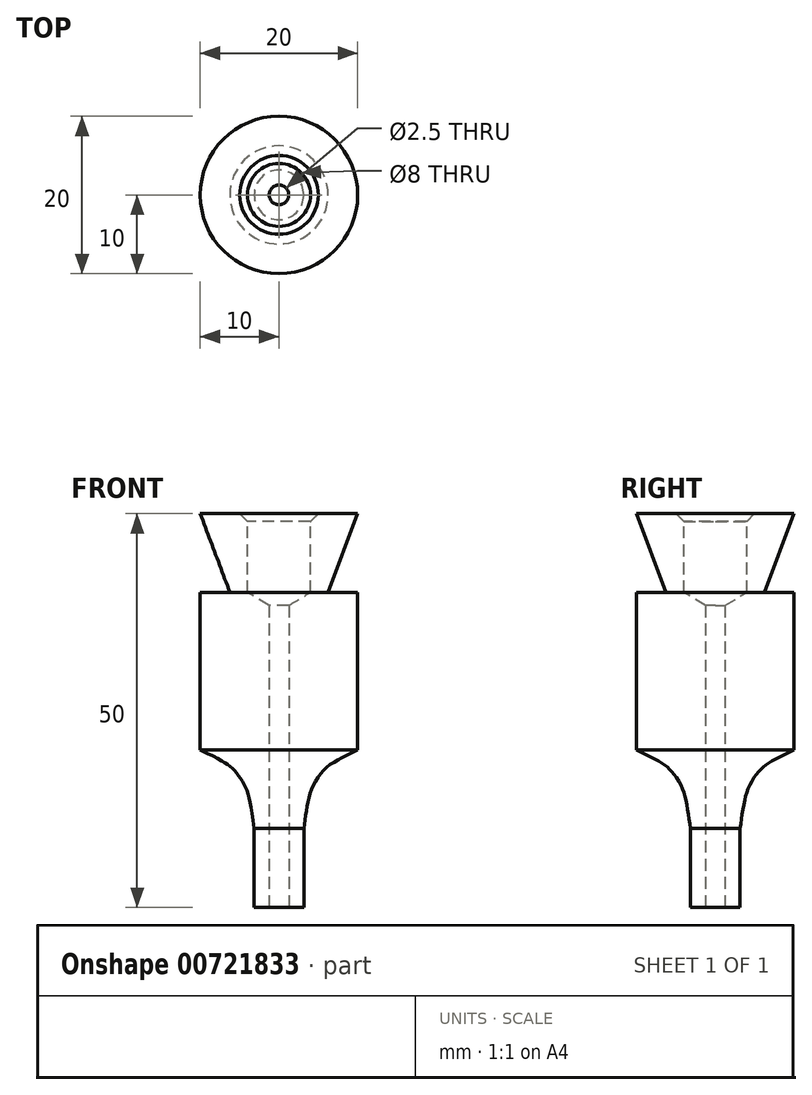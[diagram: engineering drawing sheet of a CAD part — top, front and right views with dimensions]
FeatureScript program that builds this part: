
annotation { "Feature Type Name" : "Feature", "Feature Type Description" : "" }
export const myFeature = defineFeature(function(context is Context, id is Id, definition is map)
    precondition{}
    {
        {
            var Q0;
            Q0=qCreatedBy(makeId("Front.planeOp"),FACE);
            var sketch = newSketch(context, id + "F0", { "sketchPlane" : qUnion([Q0])});
            skLineSegment(sketch, "E0", {"start": v(10, 0) * mm, "end": v(6.24, -10) * mm});
            skLineSegment(sketch, "E1", {"start": v(6.24, -10) * mm, "end": v(10, -10) * mm});
            skLineSegment(sketch, "E2", {"start": v(10, -10) * mm, "end": v(10, -30) * mm});
            skLineSegment(sketch, "E3", {"start": v(3.15, -50) * mm, "end": v(0, -50) * mm});
            skLineSegment(sketch, "E4", {"start": v(0, -50) * mm, "end": v(0, 0) * mm});
            skLineSegment(sketch, "E5", {"start": v(3.15, -50) * mm, "end": v(3.15, -30) * mm});
            skLineSegment(sketch, "E6", {"start": v(3.15, -30) * mm, "end": v(10, -30) * mm});
            skLineSegment(sketch, "E7", {"start": v(10, -10) * mm, "end": v(10, 0) * mm, "construction": true});
            skLineSegment(sketch, "E8", {"start": v(10, 0) * mm, "end": v(0, 0) * mm});
            skFitSpline(sketch, "E9", {"points": [v(10, -30) * mm, v(5.88, -32.4) * mm, v(4.43, -34.37) * mm, v(3.15, -40) * mm], "startDerivative": vector(-21.91, -10.8) * mm, "endDerivative": vector(-3.54, -25.17) * mm});
            skSolve(sketch);
        }
        {
            var Q0;
            Q0 = qSketchRegion(id + "F0", true);
            var Q1;
            Q1=sQuery(id+"F0.wireOp",EDGE,"E4");
            revolve(context, id + "F1", {"surfaceOperationType" : NewSurfaceOperationType.NEW, "entities" : qUnion([Q0]), "axis" : qUnion([Q1]), "revolveType" : RevolveType.FULL});
        }
        {
            var Q0;
            Q0=makeQuery(id+"F1.opRevolve","SWEPT_FACE",FACE,{"disambiguationData":[OSD([sQuery(id+"F0.wireOp",EDGE,"E3")])]});
            var sketch = newSketch(context, id + "F2", { "sketchPlane" : qUnion([Q0])});
            skCircle(sketch, "E10", {"center": v(0, 0) * mm, "radius": 1.25 * mm});
            skSolve(sketch);
        }
        {
            var Q0;
            Q0 = qSketchRegion(id + "F2", true);
            extrude(context, id + "F3", {"entities" : qUnion([Q0]), "operationType" : NewBodyOperationType.REMOVE, "endBound" : BoundingType.THROUGH_ALL, "oppositeDirection" : true, "depth" : 25 * mm, "offsetDistance" : 25 * mm});
        }
        {
            var Q0;
            Q0=makeQuery(id+"F1.opRevolve","SWEPT_FACE",FACE,{"disambiguationData":[OSD([sQuery(id+"F0.wireOp",EDGE,"E3")])]});
            var sketch = newSketch(context, id + "F4", { "sketchPlane" : qUnion([Q0])});
            skCircle(sketch, "E11", {"center": v(0, 0) * mm, "radius": 2 * mm});
            skSolve(sketch);
        }
        {
            var Q0;
            Q0 = qSketchRegion(id + "F4", true);
            extrude(context, id + "F5", {"entities" : qUnion([Q0]), "operationType" : NewBodyOperationType.REMOVE, "depth" : 35 * mm, "offsetDistance" : 25 * mm});
        }
        {
            var Q0;
            Q0=makeQuery(id+"F1.opRevolve","SWEPT_FACE",FACE,{"disambiguationData":[OSD([sQuery(id+"F0.wireOp",EDGE,"E8")])]});
            var sketch = newSketch(context, id + "F6", { "sketchPlane" : qUnion([Q0])});
            skPoint(sketch, "E12", {"position": v(0, 0) * mm});
            skSolve(sketch);
        }
        {
            var Q0;
            Q0=sQuery(id+"F6.wireOp",VERTEX,"E12");
            var Q1;
            Q1=makeQuery(id+"F1.opRevolve","SWEPT_BODY",BODY,{"disambiguationData":[OSD([sQuery(id+"F0.wireOp",EDGE,"E0"),sQuery(id+"F0.wireOp",EDGE,"E1"),sQuery(id+"F0.wireOp",EDGE,"E2"),sQuery(id+"F0.wireOp",EDGE,"E3"),sQuery(id+"F0.wireOp",EDGE,"E4"),sQuery(id+"F0.wireOp",EDGE,"E5"),sQuery(id+"F0.wireOp",EDGE,"E6"),sQuery(id+"F0.wireOp",EDGE,"E8")])]});
            hole(context, id + "F7", {"style" : HoleStyle.C_SINK, "endStyle" : HoleEndStyle.BLIND, "holeDiameter" : 8 * mm, "cSinkDiameter" : 10 * mm, "cSinkAngle" : 90 * degree, "majorDiameter" : 5 * mm, "holeDepth" : 10 * mm, "isTappedThrough" : true, "tappedDepth" : 12 * mm, "tapClearance" : 3, "startFromSketch" : true, "locations" : qUnion([Q0]), "scope" : qUnion([Q1])});
        }
    });
